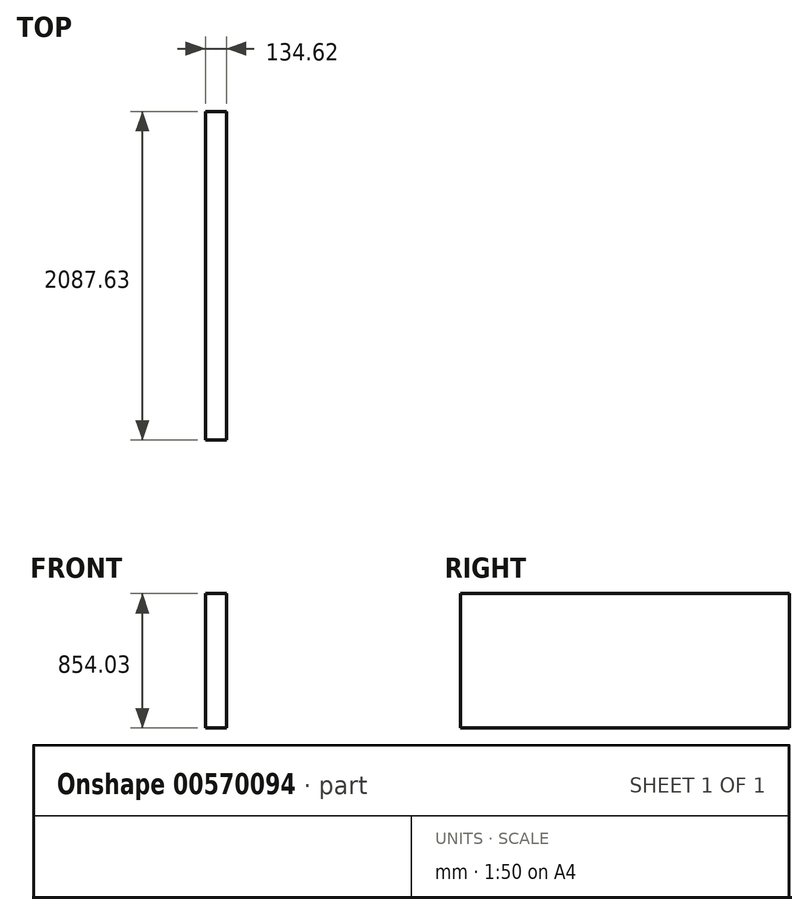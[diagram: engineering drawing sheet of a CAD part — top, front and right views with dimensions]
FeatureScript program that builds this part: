
annotation { "Feature Type Name" : "Feature", "Feature Type Description" : "" }
export const myFeature = defineFeature(function(context is Context, id is Id, definition is map)
    precondition{}
    {
        {
            var Q0;
            Q0=qCreatedBy(makeId("Right.planeOp"),FACE);
            var sketch = newSketch(context, id + "F0", { "sketchPlane" : qUnion([Q0])});
            skLineSegment(sketch, "E0.bottom", {"start": v(-461.56, -18.5) * mm, "end": v(1626.07, -18.5) * mm});
            skLineSegment(sketch, "E0.top", {"start": v(-461.56, -872.53) * mm, "end": v(1626.07, -872.53) * mm});
            skLineSegment(sketch, "E0.left", {"start": v(-461.56, -18.5) * mm, "end": v(-461.56, -872.53) * mm});
            skLineSegment(sketch, "E0.right", {"start": v(1626.07, -18.5) * mm, "end": v(1626.07, -872.53) * mm});
            skPoint(sketch, "E0.middle", {"position": v(582.25, -445.51) * mm});
            skSolve(sketch);
        }
        {
            var Q0;
            Q0=makeQuery(id+"F0.imprint","IMPRINT",FACE,{"disambiguationData":[TD([[makeQuery(id+"F0.imprint","IMPRINT",EDGE,{"derivedFrom":sQuery(id+"F0.wireOp",EDGE,"E0.bottom")}),-1.0]])]});
            extrude(context, id + "F1", {"entities" : qUnion([Q0]), "depth" : 134.62 * mm, "offsetDistance" : 25.4 * mm});
        }
    });
